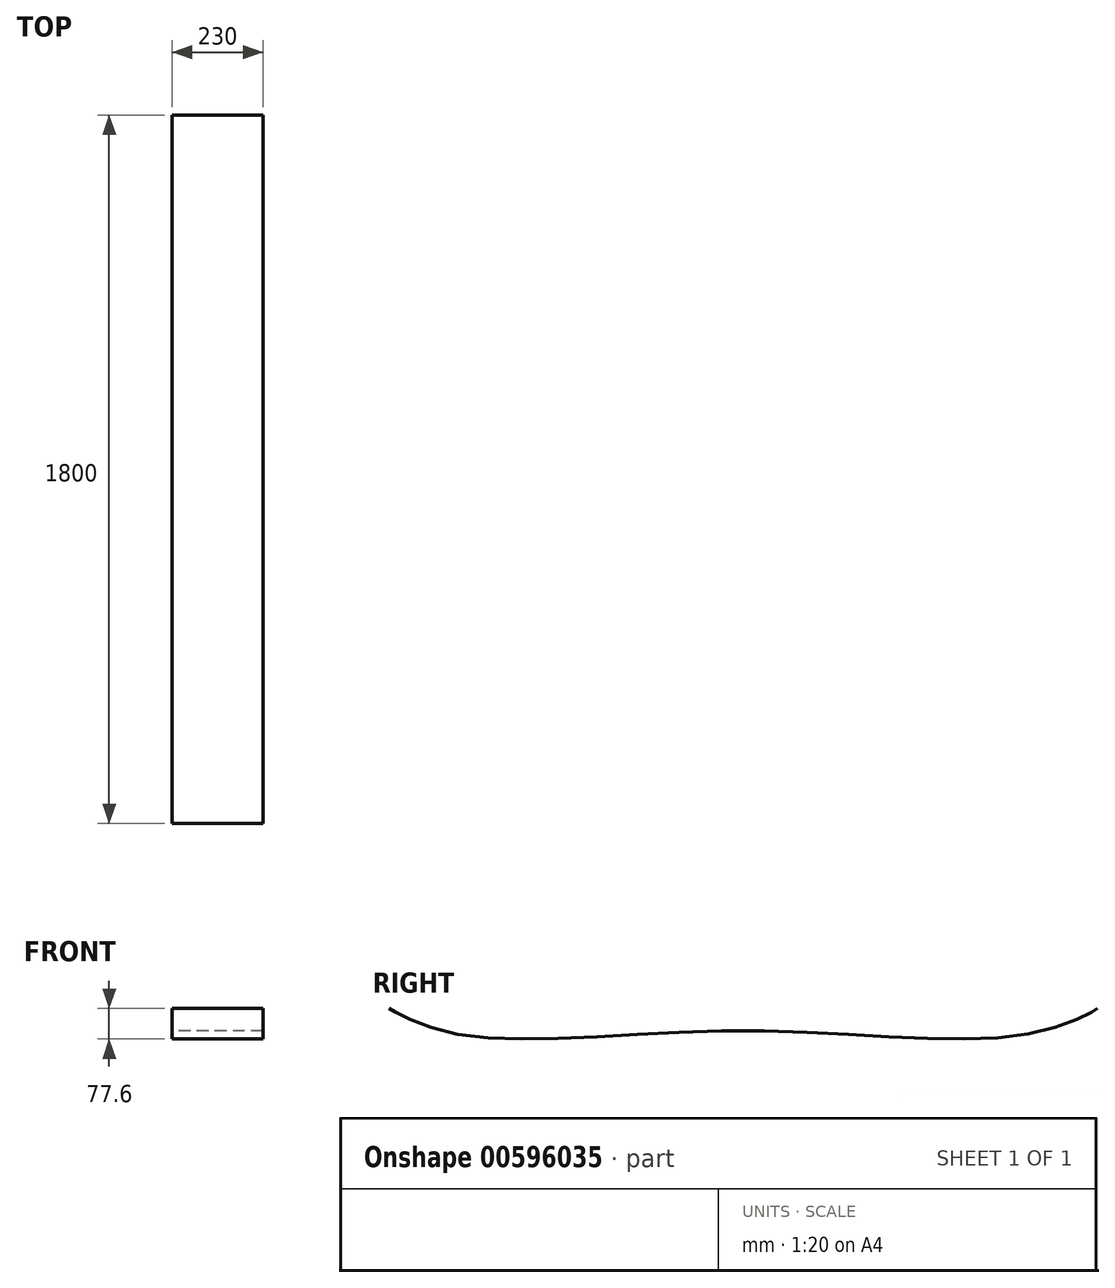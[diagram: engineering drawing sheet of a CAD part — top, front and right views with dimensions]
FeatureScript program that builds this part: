
annotation { "Feature Type Name" : "Feature", "Feature Type Description" : "" }
export const myFeature = defineFeature(function(context is Context, id is Id, definition is map)
    precondition{}
    {
        {
            var Q0;
            Q0=qCreatedBy(makeId("Right.planeOp"),FACE);
            var sketch = newSketch(context, id + "F0", { "sketchPlane" : qUnion([Q0])});
            skPoint(sketch, "E0", {"position": v(0, 60) * mm});
            skPoint(sketch, "E1", {"position": v(150, 0) * mm});
            skPoint(sketch, "E2", {"position": v(900, 3.5) * mm});
            skPoint(sketch, "E3", {"position": v(1650, 0) * mm});
            skPoint(sketch, "E4", {"position": v(1800, 60) * mm});
            skFitSpline(sketch, "E5", {"points": [v(0, 60) * mm, v(150, 0) * mm, v(900, 3.5) * mm, v(1650, 0) * mm, v(1800, 60) * mm], "startDerivative": vector(90.64, -54.03) * mm, "endDerivative": vector(49, 64.94) * mm});
            skSolve(sketch);
        }
        {
            var Q0;
            Q0=sQuery(id+"F0.wireOp",EDGE,"E5");
            extrude(context, id + "F1", {"bodyType" : ToolBodyType.SURFACE, "surfaceEntities" : qUnion([Q0]), "depth" : 230 * mm, "offsetDistance" : 25 * mm});
        }
    });
